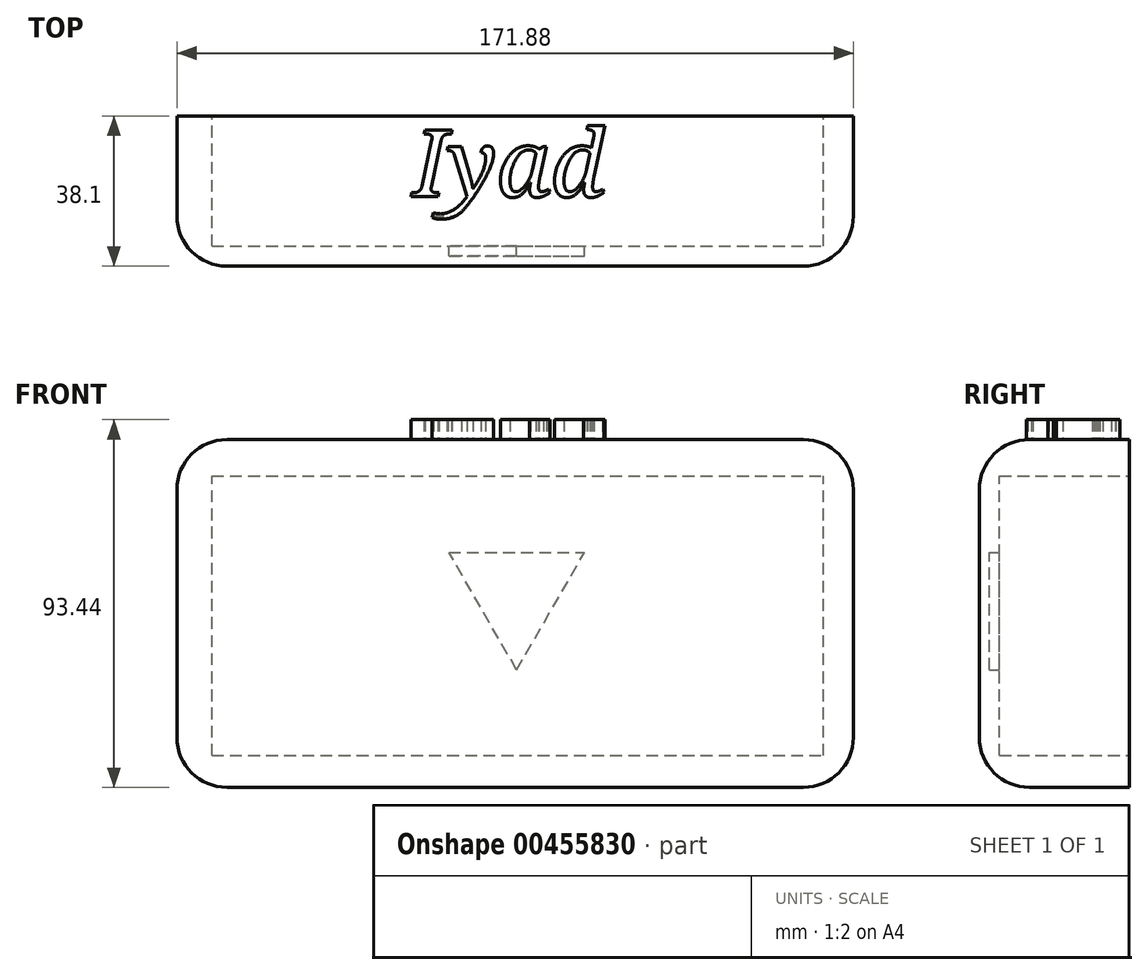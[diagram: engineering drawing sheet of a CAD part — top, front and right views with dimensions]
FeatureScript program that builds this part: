
annotation { "Feature Type Name" : "Feature", "Feature Type Description" : "" }
export const myFeature = defineFeature(function(context is Context, id is Id, definition is map)
    precondition{}
    {
        {
            var Q0;
            Q0=qCreatedBy(makeId("Front.planeOp"),FACE);
            var sketch = newSketch(context, id + "F0", { "sketchPlane" : qUnion([Q0])});
            skLineSegment(sketch, "E0.bottom", {"start": v(-99.3, 40.87) * mm, "end": v(72.59, 40.87) * mm});
            skLineSegment(sketch, "E0.top", {"start": v(-99.3, -47.49) * mm, "end": v(72.59, -47.49) * mm});
            skLineSegment(sketch, "E0.left", {"start": v(-99.3, 40.87) * mm, "end": v(-99.3, -47.49) * mm});
            skLineSegment(sketch, "E0.right", {"start": v(72.59, 40.87) * mm, "end": v(72.59, -47.49) * mm});
            skSolve(sketch);
        }
        {
            var Q0;
            Q0 = qSketchRegion(id + "F0", true);
            extrude(context, id + "F1", {"entities" : qUnion([Q0]), "depth" : 38.1 * mm});
        }
        {
            var Q0;
            Q0=makeQuery(id+"F1.opExtrude","SWEPT_EDGE",EDGE,{"disambiguationData":[OSD([sQuery(id+"F0.wireOp",EDGE,"E0.bottom"),sQuery(id+"F0.wireOp",EDGE,"E0.left")])]});
            var Q1;
            Q1=makeQuery(id+"F1.opExtrude","SWEPT_EDGE",EDGE,{"disambiguationData":[OSD([sQuery(id+"F0.wireOp",EDGE,"E0.bottom"),sQuery(id+"F0.wireOp",EDGE,"E0.right")])]});
            var Q2;
            Q2=makeQuery(id+"F1.opExtrude","SWEPT_EDGE",EDGE,{"disambiguationData":[OSD([sQuery(id+"F0.wireOp",EDGE,"E0.top"),sQuery(id+"F0.wireOp",EDGE,"E0.left")])]});
            var Q3;
            Q3=makeQuery(id+"F1.opExtrude","SWEPT_EDGE",EDGE,{"disambiguationData":[OSD([sQuery(id+"F0.wireOp",EDGE,"E0.top"),sQuery(id+"F0.wireOp",EDGE,"E0.right")])]});
            var Q4;
            Q4=makeQuery(id+"F1.opExtrude","CAP_FACE",FACE,{"disambiguationData":[OSD([sQuery(id+"F0.wireOp",EDGE,"E0.bottom"),sQuery(id+"F0.wireOp",EDGE,"E0.top"),sQuery(id+"F0.wireOp",EDGE,"E0.left"),sQuery(id+"F0.wireOp",EDGE,"E0.right")])],"isStart":false});
            fillet(context, id + "F2", {"entities" : qUnion([Q0, Q1, Q2, Q3, Q4]), "radius" : 12.7 * mm, "tangentPropagation" : true, "allowEdgeOverflow" : false});
        }
        {
            var Q0;
            Q0=makeQuery(id+"F1.opExtrude","CAP_FACE",FACE,{"disambiguationData":[OSD([sQuery(id+"F0.wireOp",EDGE,"E0.bottom"),sQuery(id+"F0.wireOp",EDGE,"E0.top"),sQuery(id+"F0.wireOp",EDGE,"E0.left"),sQuery(id+"F0.wireOp",EDGE,"E0.right")])],"isStart":true});
            var sketch = newSketch(context, id + "F3", { "sketchPlane" : qUnion([Q0])});
            skLineSegment(sketch, "E1.bottom", {"start": v(90.4, -39.43) * mm, "end": v(-65, -39.43) * mm});
            skLineSegment(sketch, "E1.top", {"start": v(90.4, 31.66) * mm, "end": v(-65, 31.66) * mm});
            skLineSegment(sketch, "E1.left", {"start": v(90.4, -39.43) * mm, "end": v(90.4, 31.66) * mm});
            skLineSegment(sketch, "E1.right", {"start": v(-65, -39.43) * mm, "end": v(-65, 31.66) * mm});
            skSolve(sketch);
        }
        {
            var Q0;
            Q0=makeQuery(id+"F3.imprint","IMPRINT",FACE,{"disambiguationData":[TD([[makeQuery(id+"F3.imprint","IMPRINT",EDGE,{"derivedFrom":sQuery(id+"F3.wireOp",EDGE,"E1.bottom")}),-1.0]])]});
            extrude(context, id + "F4", {"entities" : qUnion([Q0]), "operationType" : NewBodyOperationType.REMOVE, "oppositeDirection" : true, "depth" : 33.02 * mm});
        }
        {
            var Q0;
            Q0=makeQuery(id+"F1.opExtrude","SWEPT_FACE",FACE,{"disambiguationData":[OSD([sQuery(id+"F0.wireOp",EDGE,"E0.bottom")])]});
            var sketch = newSketch(context, id + "F5", { "sketchPlane" : qUnion([Q0])});
            skText(sketch, "E2", { "text": "Iyad ", "fontName": "NotoSerif-Italic.ttf"});
            const initialGuessF5  = {"E2": [-0.03933, -0.02047, 1, 0, 0.01708]};
            skSetInitialGuess(sketch, initialGuessF5);
            skSolve(sketch);
        }
        {
            var Q0;
            Q0 = qSketchRegion(id + "F5", true);
            extrude(context, id + "F6", {"entities" : qUnion([Q0]), "operationType" : NewBodyOperationType.ADD, "depth" : 5.08 * mm});
        }
        {
            var Q0;
            Q0=makeQuery(id+"F4.boolean.opBoolean","COPY",FACE,{"derivedFrom":makeQuery(id+"F4.opExtrude","CAP_FACE",FACE,{"disambiguationData":[OSD([sQuery(id+"F3.wireOp",EDGE,"E1.bottom"),sQuery(id+"F3.wireOp",EDGE,"E1.top"),sQuery(id+"F3.wireOp",EDGE,"E1.left"),sQuery(id+"F3.wireOp",EDGE,"E1.right")])],"isStart":false})});
            var sketch = newSketch(context, id + "F7", { "sketchPlane" : qUnion([Q0])});
            skLineSegment(sketch, "E3", {"start": v(30.2, 12.23) * mm, "end": v(-4.3, 12.23) * mm});
            skLineSegment(sketch, "E4", {"start": v(12.95, -17.65) * mm, "end": v(-4.3, 12.23) * mm});
            skLineSegment(sketch, "E5", {"start": v(12.95, -17.65) * mm, "end": v(30.2, 12.23) * mm});
            skSolve(sketch);
        }
        {
            var Q0;
            Q0=makeQuery(id+"F7.imprint","IMPRINT",FACE,{"disambiguationData":[TD([[makeQuery(id+"F7.imprint","IMPRINT",EDGE,{"derivedFrom":sQuery(id+"F7.wireOp",EDGE,"E3")}),1.0]])]});
            extrude(context, id + "F8", {"entities" : qUnion([Q0]), "operationType" : NewBodyOperationType.REMOVE, "oppositeDirection" : true, "depth" : 2.54 * mm});
        }
    });
